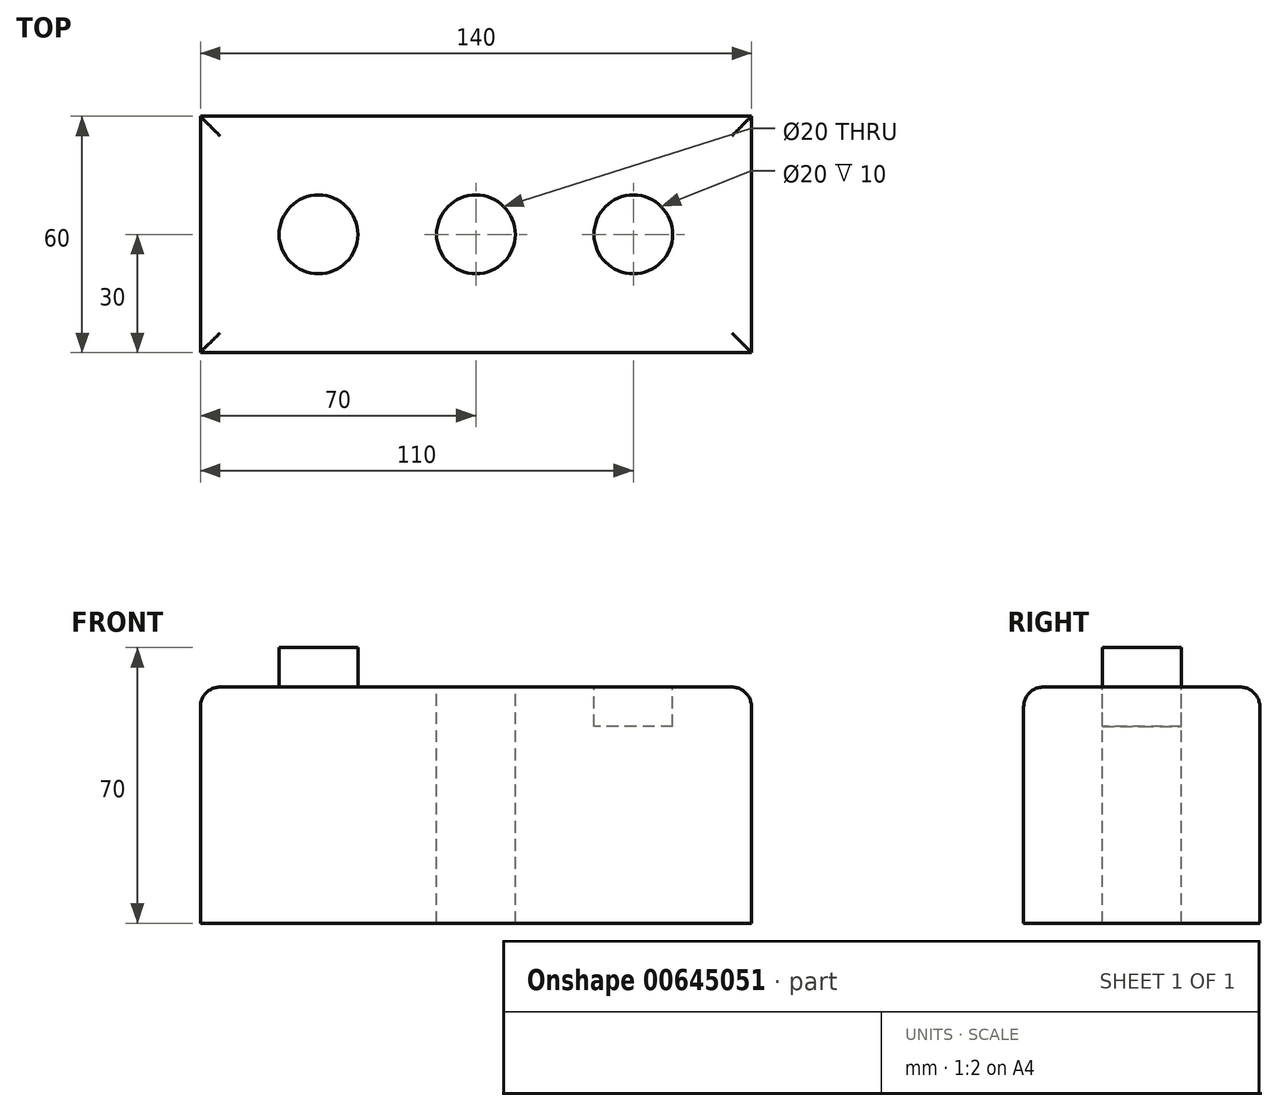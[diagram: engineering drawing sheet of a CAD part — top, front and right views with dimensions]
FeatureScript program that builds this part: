
annotation { "Feature Type Name" : "Feature", "Feature Type Description" : "" }
export const myFeature = defineFeature(function(context is Context, id is Id, definition is map)
    precondition{}
    {
        {
            var Q0;
            Q0=qCreatedBy(makeId("Top.planeOp"),FACE);
            var sketch = newSketch(context, id + "F0", { "sketchPlane" : qUnion([Q0])});
            skLineSegment(sketch, "E0.bottom", {"start": v(70, -30) * mm, "end": v(-70, -30) * mm});
            skLineSegment(sketch, "E0.top", {"start": v(70, 30) * mm, "end": v(-70, 30) * mm});
            skLineSegment(sketch, "E0.left", {"start": v(70, -30) * mm, "end": v(70, 30) * mm});
            skLineSegment(sketch, "E0.right", {"start": v(-70, -30) * mm, "end": v(-70, 30) * mm});
            skPoint(sketch, "E0.middle", {"position": v(0, 0) * mm});
            skSolve(sketch);
        }
        {
            var Q0;
            Q0 = qSketchRegion(id + "F0", true);
            extrude(context, id + "F1", {"entities" : qUnion([Q0]), "depth" : 60 * mm, "offsetDistance" : 25 * mm});
        }
        {
            var Q0;
            Q0=makeQuery(id+"F1.opExtrude","CAP_FACE",FACE,{"disambiguationData":[OSD([sQuery(id+"F0.wireOp",EDGE,"E0.bottom"),sQuery(id+"F0.wireOp",EDGE,"E0.top"),sQuery(id+"F0.wireOp",EDGE,"E0.left"),sQuery(id+"F0.wireOp",EDGE,"E0.right")])],"isStart":false});
            var sketch = newSketch(context, id + "F2", { "sketchPlane" : qUnion([Q0])});
            skCircle(sketch, "E1", {"center": v(-40, 0) * mm, "radius": 10 * mm});
            skSolve(sketch);
        }
        {
            var Q0;
            Q0=makeQuery(id+"F2.imprint","IMPRINT",FACE,{"disambiguationData":[TD([[makeQuery(id+"F2.imprint","IMPRINT",EDGE,{"derivedFrom":sQuery(id+"F2.wireOp",EDGE,"E1")}),-1.0]])]});
            var sketch = newSketch(context, id + "F3", { "sketchPlane" : qUnion([Q0])});
            skCircle(sketch, "E2", {"center": v(40, 0) * mm, "radius": 10 * mm});
            skSolve(sketch);
        }
        {
            var Q0;
            Q0=makeQuery(id+"F2.imprint","IMPRINT",FACE,{"disambiguationData":[TD([[makeQuery(id+"F2.imprint","IMPRINT",EDGE,{"derivedFrom":sQuery(id+"F2.wireOp",EDGE,"E1")}),-1.0]])]});
            var sketch = newSketch(context, id + "F4", { "sketchPlane" : qUnion([Q0])});
            skCircle(sketch, "E3", {"center": v(0, 0) * mm, "radius": 10 * mm});
            skSolve(sketch);
        }
        {
            var Q0;
            Q0 = qSketchRegion(id + "F2", true);
            extrude(context, id + "F5", {"entities" : qUnion([Q0]), "operationType" : NewBodyOperationType.ADD, "depth" : 10 * mm, "offsetDistance" : 25 * mm});
        }
        {
            var Q0;
            Q0 = qSketchRegion(id + "F4", true);
            extrude(context, id + "F6", {"entities" : qUnion([Q0]), "operationType" : NewBodyOperationType.REMOVE, "oppositeDirection" : true, "depth" : 102.5 * mm, "offsetDistance" : 25 * mm});
        }
        {
            var Q0;
            Q0 = qSketchRegion(id + "F3", true);
            extrude(context, id + "F7", {"entities" : qUnion([Q0]), "operationType" : NewBodyOperationType.REMOVE, "oppositeDirection" : true, "depth" : 10 * mm, "offsetDistance" : 25 * mm});
        }
        {
            var Q0;
            Q0=makeQuery(id+"F1.opExtrude","CAP_EDGE",EDGE,{"disambiguationData":[OSD([sQuery(id+"F0.wireOp",EDGE,"E0.top")])],"isStart":false});
            var Q1;
            Q1=makeQuery(id+"F1.opExtrude","CAP_EDGE",EDGE,{"disambiguationData":[OSD([sQuery(id+"F0.wireOp",EDGE,"E0.right")])],"isStart":false});
            var Q2;
            Q2=makeQuery(id+"F1.opExtrude","CAP_EDGE",EDGE,{"disambiguationData":[OSD([sQuery(id+"F0.wireOp",EDGE,"E0.bottom")])],"isStart":false});
            var Q3;
            Q3=makeQuery(id+"F1.opExtrude","CAP_EDGE",EDGE,{"disambiguationData":[OSD([sQuery(id+"F0.wireOp",EDGE,"E0.left")])],"isStart":false});
            fillet(context, id + "F8", {"entities" : qUnion([Q0, Q1, Q2, Q3]), "radius" : 5 * mm, "tangentPropagation" : true, "allowEdgeOverflow" : false});
        }
    });
